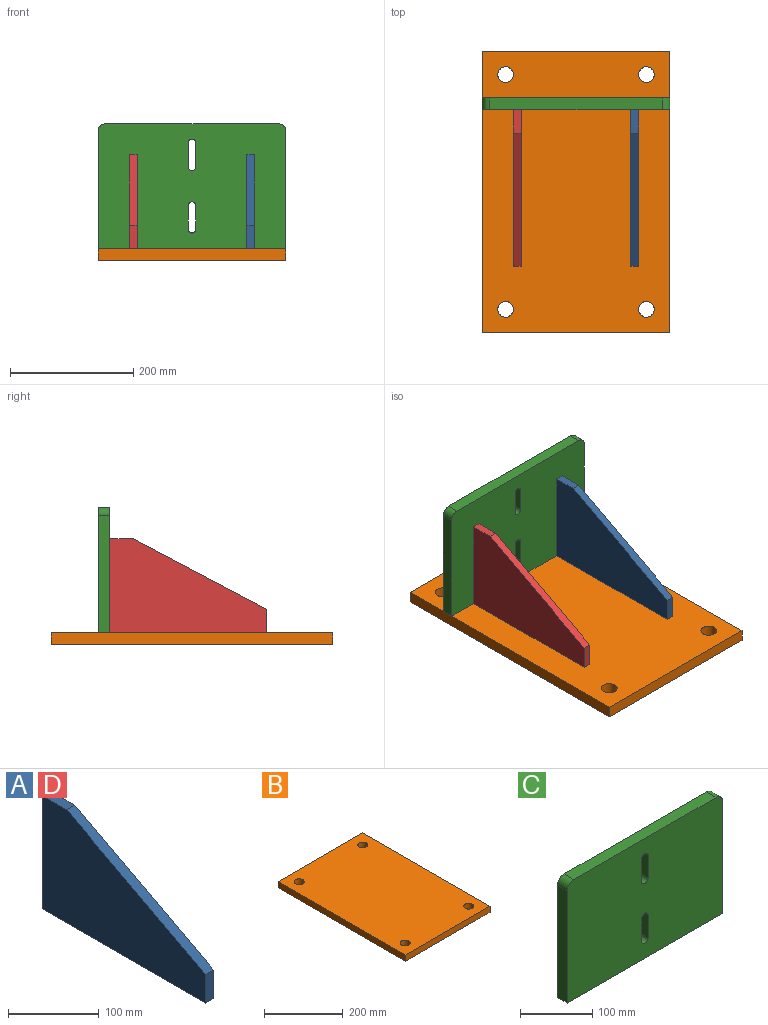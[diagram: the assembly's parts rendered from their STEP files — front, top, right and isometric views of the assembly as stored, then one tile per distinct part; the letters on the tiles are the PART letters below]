
ASSEMBLY  parts=4 mates=3
PART A: 7 faces, bbox 12.7x254x152.4 mm
  f0: plane 152.4x12.7mm, normal (0,1,0), area 1935.5mm2, adj f1,f4,f5,f6
  f1: plane 38.1x12.7mm, normal (0,0,1), area 483.9mm2, adj f0,f2,f5,f6
  f2: plane 215.9x114.3mm, normal (0,-0.47,0.88), area 3102.5mm2, adj f1,f3,f5,f6
  f3: plane 38.1x12.7mm, normal (0,-1,0), area 483.9mm2, adj f2,f4,f5,f6
  f4: plane 254x12.7mm, normal (0,0,-1), area 3225.8mm2, adj f0,f3,f5,f6
  f5: plane 254x152.4mm, normal (1,0,0), area 26370.9mm2, adj f0,f1,f2,f3,f4
  f6: plane 254x152.4mm, normal (-1,0,0), area 26370.9mm2, adj f0,f1,f2,f3,f4
PART B: 10 faces, bbox 304.8x457.2x19.1 mm
  f0: plane 457.2x19.05mm, normal (-1,0,0), area 8709.7mm2, adj f1,f3,f8,f9
  f1: plane 304.8x19.05mm, normal (0,-1,0), area 5806.4mm2, adj f0,f2,f8,f9
  f2: plane 457.2x19.05mm, normal (1,0,0), area 8709.7mm2, adj f1,f3,f8,f9
  f3: plane 304.8x19.05mm, normal (0,1,0), area 5806.4mm2, adj f0,f2,f8,f9
  f4: cylinder r=12.7mm len=25.4mm, axis (0,0,-1), area 1520.1mm2, adj f8,f9
  f5: cylinder r=12.7mm len=25.4mm, axis (0,0,-1), area 1520.1mm2, adj f8,f9
  f6: cylinder r=12.7mm len=25.4mm, axis (0,0,-1), area 1520.1mm2, adj f8,f9
  f7: cylinder r=12.7mm len=25.4mm, axis (0,0,-1), area 1520.1mm2, adj f8,f9
  f8: plane 457.2x304.8mm, normal (0,0,1), area 137327.7mm2, adj f0,f1,f2,f3,f4,f5,f6,f7
  f9: plane 457.2x304.8mm, normal (0,0,-1), area 137327.7mm2, adj f0,f1,f2,f3,f4,f5,f6,f7
PART C: 16 faces, bbox 304.8x19.1x203.2 mm
  f0: plane 38.1x19.05mm, normal (-1,0,0), area 725.8mm2, adj f1,f13,f14,f15
  f1: cylinder r=6.35mm len=19.05mm, axis (0,1,0), area 380mm2, adj f0,f2,f14,f15
  f2: plane 38.1x19.05mm, normal (1,0,0), area 725.8mm2, adj f1,f13,f14,f15
  f3: plane 38.1x19.05mm, normal (-1,0,0), area 725.8mm2, adj f4,f11,f14,f15
  f4: cylinder r=6.35mm len=19.05mm, axis (0,1,0), area 380mm2, adj f3,f5,f14,f15
  f5: plane 38.1x19.05mm, normal (1,0,0), area 725.8mm2, adj f4,f11,f14,f15
  f6: plane 190.5x19.05mm, normal (-1,0,0), area 3629mm2, adj f7,f12,f14,f15
  f7: plane 304.8x19.05mm, normal (0,0,-1), area 5806.4mm2, adj f6,f8,f14,f15
  f8: plane 190.5x19.05mm, normal (1,0,0), area 3629mm2, adj f7,f9,f14,f15
  f9: cylinder r=12.7mm len=19.05mm, axis (0,1,0), area 380mm2, adj f8,f10,f14,f15
  f10: plane 279.4x19.05mm, normal (0,0,1), area 5322.6mm2, adj f9,f12,f14,f15
  f11: cylinder r=6.35mm len=19.05mm, axis (0,1,0), area 380mm2, adj f3,f5,f14,f15
  f12: cylinder r=12.7mm len=19.05mm, axis (0,1,0), area 380mm2, adj f6,f10,f14,f15
  f13: cylinder r=6.35mm len=19.05mm, axis (0,1,0), area 380mm2, adj f0,f2,f14,f15
  f14: plane 304.8x203.2mm, normal (0,-1,0), area 60645mm2, adj f0,f1,f2,f3,f4,f5,f6,f7
  f15: plane 304.8x203.2mm, normal (0,1,0), area 60645mm2, adj f0,f1,f2,f3,f4,f5,f6,f7
PART D: same geometry as A
PLACE A t=(292.21,-41.37,-11.74)mm
PLACE B at identity fixed
PLACE C t=(203.31,-286.76,120.65)mm
PLACE D t=(101.71,-41.37,-11.74)mm
MATE fastened D.f0 <-> C.f14  axis (0,1,0) through (101.71,-305.81,19.05)mm
MATE fastened C.f7 <-> B.f8  axis (0,0,-1) through (203.31,-286.76,19.05)mm
MATE fastened A.f0 <-> C.f14  axis (0,1,0) through (304.91,-305.81,19.05)mm
